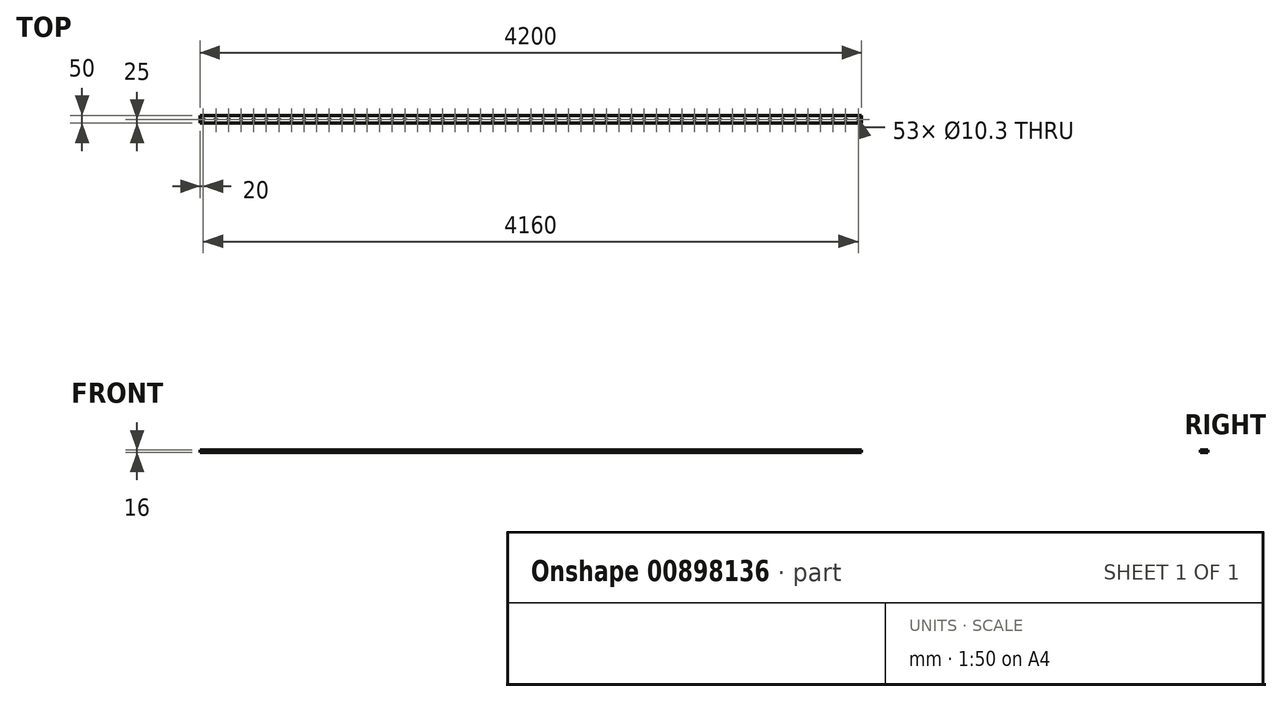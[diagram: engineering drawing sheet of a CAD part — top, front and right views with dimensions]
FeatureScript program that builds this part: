
annotation { "Feature Type Name" : "Feature", "Feature Type Description" : "" }
export const myFeature = defineFeature(function(context is Context, id is Id, definition is map)
    precondition{}
    {
        {
            var Q0;
            Q0=qCreatedBy(makeId("Top.planeOp"),FACE);
            var sketch = newSketch(context, id + "F0", { "sketchPlane" : qUnion([Q0])});
            skLineSegment(sketch, "E0.bottom", {"start": v(2100, 25) * mm, "end": v(-2100, 25) * mm});
            skLineSegment(sketch, "E0.top", {"start": v(2100, -25) * mm, "end": v(-2100, -25) * mm});
            skLineSegment(sketch, "E0.left", {"start": v(2100, 25) * mm, "end": v(2100, -25) * mm});
            skLineSegment(sketch, "E0.right", {"start": v(-2100, 25) * mm, "end": v(-2100, -25) * mm});
            skPoint(sketch, "E0.middle", {"position": v(0, 0) * mm});
            skSolve(sketch);
        }
        {
            var Q0;
            Q0 = qSketchRegion(id + "F0", true);
            extrude(context, id + "F1", {"entities" : qUnion([Q0]), "depth" : 16 * mm, "offsetDistance" : 25 * mm});
        }
        {
            var Q0;
            Q0=makeQuery(id+"F1.opExtrude","CAP_FACE",FACE,{"disambiguationData":[OSD([sQuery(id+"F0.wireOp",EDGE,"E0.bottom"),sQuery(id+"F0.wireOp",EDGE,"E0.top"),sQuery(id+"F0.wireOp",EDGE,"E0.left"),sQuery(id+"F0.wireOp",EDGE,"E0.right")])],"isStart":false});
            var sketch = newSketch(context, id + "F2", { "sketchPlane" : qUnion([Q0])});
            skLineSegment(sketch, "E1.0", {"start": v(-2100, 25) * mm, "end": v(-2100, -25) * mm, "construction": true});
            skPoint(sketch, "E2", {"position": v(-2080, 0) * mm});
            skPoint(sketch, "E3.1.0.0", {"position": v(-2000, 0) * mm});
            skPoint(sketch, "E3.2.0.0", {"position": v(-1920, 0) * mm});
            skPoint(sketch, "E3.3.0.0", {"position": v(-1840, 0) * mm});
            skPoint(sketch, "E3.4.0.0", {"position": v(-1760, 0) * mm});
            skPoint(sketch, "E3.5.0.0", {"position": v(-1680, 0) * mm});
            skPoint(sketch, "E3.6.0.0", {"position": v(-1600, 0) * mm});
            skPoint(sketch, "E3.7.0.0", {"position": v(-1520, 0) * mm});
            skPoint(sketch, "E3.8.0.0", {"position": v(-1440, 0) * mm});
            skPoint(sketch, "E3.9.0.0", {"position": v(-1360, 0) * mm});
            skPoint(sketch, "E3.10.0.0", {"position": v(-1280, 0) * mm});
            skPoint(sketch, "E3.11.0.0", {"position": v(-1200, 0) * mm});
            skPoint(sketch, "E3.12.0.0", {"position": v(-1120, 0) * mm});
            skPoint(sketch, "E3.13.0.0", {"position": v(-1040, 0) * mm});
            skPoint(sketch, "E3.14.0.0", {"position": v(-960, 0) * mm});
            skPoint(sketch, "E3.15.0.0", {"position": v(-880, 0) * mm});
            skPoint(sketch, "E3.16.0.0", {"position": v(-800, 0) * mm});
            skPoint(sketch, "E3.17.0.0", {"position": v(-720, 0) * mm});
            skPoint(sketch, "E3.18.0.0", {"position": v(-640, 0) * mm});
            skPoint(sketch, "E3.19.0.0", {"position": v(-560, 0) * mm});
            skPoint(sketch, "E3.20.0.0", {"position": v(-480, 0) * mm});
            skPoint(sketch, "E3.21.0.0", {"position": v(-400, 0) * mm});
            skPoint(sketch, "E3.22.0.0", {"position": v(-320, 0) * mm});
            skPoint(sketch, "E3.23.0.0", {"position": v(-240, 0) * mm});
            skPoint(sketch, "E3.24.0.0", {"position": v(-160, 0) * mm});
            skPoint(sketch, "E3.25.0.0", {"position": v(-80, 0) * mm});
            skPoint(sketch, "E3.26.0.0", {"position": v(0, 0) * mm});
            skPoint(sketch, "E3.27.0.0", {"position": v(80, 0) * mm});
            skPoint(sketch, "E3.28.0.0", {"position": v(160, 0) * mm});
            skPoint(sketch, "E3.29.0.0", {"position": v(240, 0) * mm});
            skPoint(sketch, "E3.30.0.0", {"position": v(320, 0) * mm});
            skPoint(sketch, "E3.31.0.0", {"position": v(400, 0) * mm});
            skPoint(sketch, "E3.32.0.0", {"position": v(480, 0) * mm});
            skPoint(sketch, "E3.33.0.0", {"position": v(560, 0) * mm});
            skPoint(sketch, "E3.34.0.0", {"position": v(640, 0) * mm});
            skPoint(sketch, "E3.35.0.0", {"position": v(720, 0) * mm});
            skPoint(sketch, "E3.36.0.0", {"position": v(800, 0) * mm});
            skPoint(sketch, "E3.37.0.0", {"position": v(880, 0) * mm});
            skPoint(sketch, "E3.38.0.0", {"position": v(960, 0) * mm});
            skPoint(sketch, "E3.39.0.0", {"position": v(1040, 0) * mm});
            skPoint(sketch, "E3.40.0.0", {"position": v(1120, 0) * mm});
            skPoint(sketch, "E3.41.0.0", {"position": v(1200, 0) * mm});
            skPoint(sketch, "E3.42.0.0", {"position": v(1280, 0) * mm});
            skPoint(sketch, "E3.43.0.0", {"position": v(1360, 0) * mm});
            skPoint(sketch, "E3.44.0.0", {"position": v(1440, 0) * mm});
            skPoint(sketch, "E3.45.0.0", {"position": v(1520, 0) * mm});
            skPoint(sketch, "E3.46.0.0", {"position": v(1600, 0) * mm});
            skPoint(sketch, "E3.47.0.0", {"position": v(1680, 0) * mm});
            skPoint(sketch, "E3.48.0.0", {"position": v(1760, 0) * mm});
            skPoint(sketch, "E3.49.0.0", {"position": v(1840, 0) * mm});
            skPoint(sketch, "E3.50.0.0", {"position": v(1920, 0) * mm});
            skPoint(sketch, "E3.51.0.0", {"position": v(2000, 0) * mm});
            skPoint(sketch, "E3.52.0.0", {"position": v(2080, 0) * mm});
            skLineSegment(sketch, "E3.direction1", {"start": v(-2080, 0) * mm, "end": v(-2000, 0) * mm, "construction": true});
            skLineSegment(sketch, "E4", {"start": v(100, 133.47) * mm, "end": v(100, -162.28) * mm, "construction": true});
            skLineSegment(sketch, "E5.0", {"start": v(2100, -25) * mm, "end": v(-2100, -25) * mm, "construction": true});
            skLineSegment(sketch, "E6.0", {"start": v(2100, 25) * mm, "end": v(-2100, 25) * mm, "construction": true});
            skLineSegment(sketch, "E7", {"start": v(-100, -187.32) * mm, "end": v(-100, 183.98) * mm, "construction": true});
            skSolve(sketch);
        }
        {
            var Q0;
            Q0=sQuery(id+"F2.wireOp",VERTEX,"E2");
            var Q1;
            Q1=sQuery(id+"F2.wireOp",VERTEX,"E3.1.0.0");
            var Q2;
            Q2=sQuery(id+"F2.wireOp",VERTEX,"E3.2.0.0");
            var Q3;
            Q3=sQuery(id+"F2.wireOp",VERTEX,"E3.3.0.0");
            var Q4;
            Q4=sQuery(id+"F2.wireOp",VERTEX,"E3.4.0.0");
            var Q5;
            Q5=sQuery(id+"F2.wireOp",VERTEX,"E3.5.0.0");
            var Q6;
            Q6=sQuery(id+"F2.wireOp",VERTEX,"E3.6.0.0");
            var Q7;
            Q7=sQuery(id+"F2.wireOp",VERTEX,"E3.7.0.0");
            var Q8;
            Q8=sQuery(id+"F2.wireOp",VERTEX,"E3.8.0.0");
            var Q9;
            Q9=sQuery(id+"F2.wireOp",VERTEX,"E3.9.0.0");
            var Q10;
            Q10=sQuery(id+"F2.wireOp",VERTEX,"E3.10.0.0");
            var Q11;
            Q11=sQuery(id+"F2.wireOp",VERTEX,"E3.11.0.0");
            var Q12;
            Q12=sQuery(id+"F2.wireOp",VERTEX,"E3.12.0.0");
            var Q13;
            Q13=sQuery(id+"F2.wireOp",VERTEX,"E3.13.0.0");
            var Q14;
            Q14=sQuery(id+"F2.wireOp",VERTEX,"E3.14.0.0");
            var Q15;
            Q15=sQuery(id+"F2.wireOp",VERTEX,"E3.15.0.0");
            var Q16;
            Q16=sQuery(id+"F2.wireOp",VERTEX,"E3.16.0.0");
            var Q17;
            Q17=sQuery(id+"F2.wireOp",VERTEX,"E3.17.0.0");
            var Q18;
            Q18=sQuery(id+"F2.wireOp",VERTEX,"E3.18.0.0");
            var Q19;
            Q19=sQuery(id+"F2.wireOp",VERTEX,"E3.19.0.0");
            var Q20;
            Q20=sQuery(id+"F2.wireOp",VERTEX,"E3.20.0.0");
            var Q21;
            Q21=sQuery(id+"F2.wireOp",VERTEX,"E3.21.0.0");
            var Q22;
            Q22=sQuery(id+"F2.wireOp",VERTEX,"E3.22.0.0");
            var Q23;
            Q23=sQuery(id+"F2.wireOp",VERTEX,"E3.23.0.0");
            var Q24;
            Q24=sQuery(id+"F2.wireOp",VERTEX,"E3.24.0.0");
            var Q25;
            Q25=sQuery(id+"F2.wireOp",VERTEX,"E3.25.0.0");
            var Q26;
            Q26=sQuery(id+"F2.wireOp",VERTEX,"E3.26.0.0");
            var Q27;
            Q27=sQuery(id+"F2.wireOp",VERTEX,"E3.27.0.0");
            var Q28;
            Q28=sQuery(id+"F2.wireOp",VERTEX,"E3.28.0.0");
            var Q29;
            Q29=sQuery(id+"F2.wireOp",VERTEX,"E3.29.0.0");
            var Q30;
            Q30=sQuery(id+"F2.wireOp",VERTEX,"E3.30.0.0");
            var Q31;
            Q31=sQuery(id+"F2.wireOp",VERTEX,"E3.31.0.0");
            var Q32;
            Q32=sQuery(id+"F2.wireOp",VERTEX,"E3.32.0.0");
            var Q33;
            Q33=sQuery(id+"F2.wireOp",VERTEX,"E3.33.0.0");
            var Q34;
            Q34=sQuery(id+"F2.wireOp",VERTEX,"E3.34.0.0");
            var Q35;
            Q35=sQuery(id+"F2.wireOp",VERTEX,"E3.35.0.0");
            var Q36;
            Q36=sQuery(id+"F2.wireOp",VERTEX,"E3.36.0.0");
            var Q37;
            Q37=sQuery(id+"F2.wireOp",VERTEX,"E3.37.0.0");
            var Q38;
            Q38=sQuery(id+"F2.wireOp",VERTEX,"E3.38.0.0");
            var Q39;
            Q39=sQuery(id+"F2.wireOp",VERTEX,"E3.39.0.0");
            var Q40;
            Q40=sQuery(id+"F2.wireOp",VERTEX,"E3.40.0.0");
            var Q41;
            Q41=sQuery(id+"F2.wireOp",VERTEX,"E3.41.0.0");
            var Q42;
            Q42=sQuery(id+"F2.wireOp",VERTEX,"E3.42.0.0");
            var Q43;
            Q43=sQuery(id+"F2.wireOp",VERTEX,"E3.43.0.0");
            var Q44;
            Q44=sQuery(id+"F2.wireOp",VERTEX,"E3.44.0.0");
            var Q45;
            Q45=sQuery(id+"F2.wireOp",VERTEX,"E3.45.0.0");
            var Q46;
            Q46=sQuery(id+"F2.wireOp",VERTEX,"E3.46.0.0");
            var Q47;
            Q47=sQuery(id+"F2.wireOp",VERTEX,"E3.47.0.0");
            var Q48;
            Q48=sQuery(id+"F2.wireOp",VERTEX,"E3.48.0.0");
            var Q49;
            Q49=sQuery(id+"F2.wireOp",VERTEX,"E3.49.0.0");
            var Q50;
            Q50=sQuery(id+"F2.wireOp",VERTEX,"E3.50.0.0");
            var Q51;
            Q51=sQuery(id+"F2.wireOp",VERTEX,"E3.52.0.0");
            var Q52;
            Q52=sQuery(id+"F2.wireOp",VERTEX,"E3.51.0.0");
            var Q53;
            Q53=makeQuery(id+"F1.opExtrude","SWEPT_BODY",BODY,{"disambiguationData":[OSD([sQuery(id+"F0.wireOp",EDGE,"E0.bottom"),sQuery(id+"F0.wireOp",EDGE,"E0.top"),sQuery(id+"F0.wireOp",EDGE,"E0.left"),sQuery(id+"F0.wireOp",EDGE,"E0.right")])]});
            hole(context, id + "F3", {"style" : HoleStyle.SIMPLE, "endStyle" : HoleEndStyle.THROUGH, "standardTappedOrClearance" : lookupTablePath({ "standard" : "ISO", "engagement" : "75%", "pitch" : "1.75 mm", "size" : "M12", "type" : "Tapped" }), "standardBlindInLast" : lookupTablePath({ "standard" : "ISO", "engagement" : "75%", "pitch" : "1.75 mm", "size" : "M12", "type" : "Tapped" }), "holeDiameter" : 10.3 * mm, "majorDiameter" : 12 * mm, "showTappedDepth" : true, "isTappedThrough" : true, "tappedDepth" : 3.9 * mm, "tapClearance" : 3, "locations" : qUnion([Q0, Q1, Q2, Q3, Q4, Q5, Q6, Q7, Q8, Q9, Q10, Q11, Q12, Q13, Q14, Q15, Q16, Q17, Q18, Q19, Q20, Q21, Q22, Q23, Q24, Q25, Q26, Q27, Q28, Q29, Q30, Q31, Q32, Q33, Q34, Q35, Q36, Q37, Q38, Q39, Q40, Q41, Q42, Q43, Q44, Q45, Q46, Q47, Q48, Q49, Q50, Q51, Q52]), "scope" : qUnion([Q53])});
        }
        {
            var Q0;
            Q0=makeQuery(id+"F1.opExtrude","SWEPT_FACE",FACE,{"disambiguationData":[OSD([sQuery(id+"F0.wireOp",EDGE,"E0.left")])]});
            cPlane(context, id + "F4", {"entities" : qUnion([Q0]), "cplaneType" : CPlaneType.OFFSET, "offset" : 2000 * mm, "oppositeDirection" : true, "width" : 150 * mm, "height" : 150 * mm});
        }
    });
